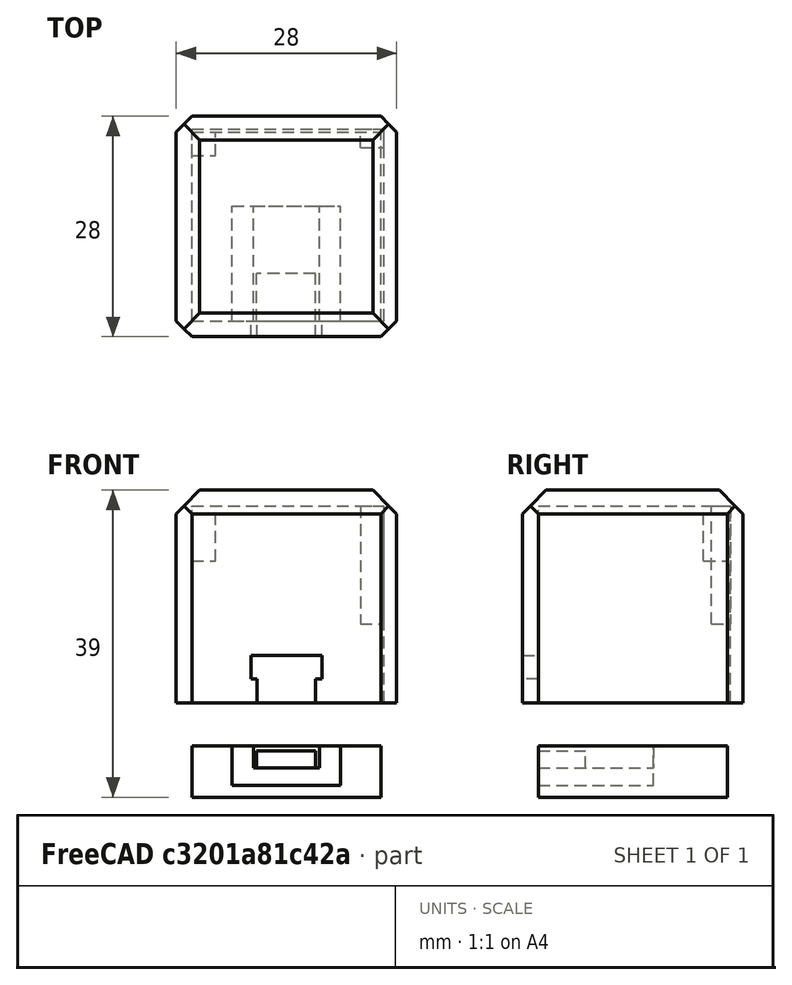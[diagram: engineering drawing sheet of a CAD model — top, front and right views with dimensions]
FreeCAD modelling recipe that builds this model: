
FCSTD DOCUMENT  (FreeCAD 0.21R33694 (Git))
Label: IR-housing
License: All rights reserved
LicenseURL: https://en.wikipedia.org/wiki/All_rights_reserved
objects: PartDesign::AdditiveBox×5, PartDesign::SubtractiveBox×5, PartDesign::Body×2, PartDesign::Chamfer×2
note: 26 computed .brp shape members not serialized (recipe doc carries the construction recipe); baked Part::Feature solids carry a one-line shape summary decoded from their .brp

FEATURE [PartDesign::AdditiveBox] Box
  AttacherType = Attacher::AttachEngine3D
  Height = 27
  Length = 28
  MapMode = 5
  Support = -> [XY_Plane]
  Width = 28
FEATURE [PartDesign::SubtractiveBox] Box001
  AttacherType = Attacher::AttachEngine3D
  AttachmentOffset = pos=(2,2,0) rot=(0,0,1;0rad)
  BaseFeature = -> Box
  Height = 25
  Length = 24.4
  MapMode = 5
  Placement = pos=(2,2,0) rot=(0,0,1;0rad)
  Support = -> [XY_Plane]
  Width = 24.4
FEATURE [PartDesign::AdditiveBox] Box002
  AttacherType = Attacher::AttachEngine3D
  AttachmentOffset = pos=(2,2,-12) rot=(0,0,1;0rad)
  Height = 6.5
  Length = 24
  MapMode = 5
  Placement = pos=(2,2,-12) rot=(0,0,1;0rad)
  Support = -> [XY_Plane001]
  Width = 24
FEATURE [PartDesign::SubtractiveBox] Box003
  AttacherType = Attacher::AttachEngine3D
  AttachmentOffset = pos=(7.1,2,-10.5) rot=(0,0,1;0rad)
  BaseFeature = -> Box002
  Height = 5
  Length = 13.8
  MapMode = 5
  Placement = pos=(7.1,2,-10.5) rot=(0,0,1;0rad)
  Support = -> [XY_Plane001]
  Width = 14.6
FEATURE [PartDesign::SubtractiveBox] Box004
  AttacherType = Attacher::AttachEngine3D
  AttachmentOffset = pos=(10.3,0,0) rot=(0,0,1;0rad)
  BaseFeature = -> Box001
  Height = 5
  Length = 7.4
  MapMode = 5
  Placement = pos=(10.3,0,0) rot=(0,0,1;0rad)
  Support = -> [XY_Plane]
  Width = 2.3
FEATURE [PartDesign::AdditiveBox] Box005
  AttacherType = Attacher::AttachEngine3D
  AttachmentOffset = pos=(9.8,2,-8.3) rot=(0,0,1;0rad)
  BaseFeature = -> Box003
  Height = 2.8
  Length = 8.4
  MapMode = 5
  Placement = pos=(9.8,2,-8.3) rot=(0,0,1;0rad)
  Support = -> [XY_Plane001]
  Width = 15.5
FEATURE [PartDesign::SubtractiveBox] Box006
  AttacherType = Attacher::AttachEngine3D
  AttachmentOffset = pos=(10.2,2,-8.5) rot=(0,0,1;0rad)
  BaseFeature = -> Box005
  Height = 2.4
  Length = 7.5
  MapMode = 5
  Placement = pos=(10.2,2,-8.5) rot=(0,0,1;0rad)
  Support = -> [XY_Plane001]
  Width = 6
FEATURE [PartDesign::Body] Body001
  Group = -> [Box002,Box003,Box005,Box006]
  Origin = -> Origin001
  Tip = -> Box006
FEATURE [PartDesign::Chamfer] Chamfer
  Angle = 45
  Base = -> Box004 [Edge2,Edge11,Edge13,Edge12]
  BaseFeature = -> Box004
  ChamferType = 0
  FlipDirection = false
  Placement = pos=(10.3,0,0) rot=(0,0,1;0rad)
  Size = 3
  Size2 = 1
  SupportTransform = false
  UseAllEdges = false
FEATURE [PartDesign::Chamfer] Chamfer001
  Angle = 45
  Base = -> Chamfer [Edge1,Edge4,Edge5,Edge24]
  BaseFeature = -> Chamfer
  ChamferType = 0
  FlipDirection = false
  Placement = pos=(10.3,0,0) rot=(0,0,1;0rad)
  Size = 2
  Size2 = 1
  SupportTransform = false
  UseAllEdges = false
FEATURE [PartDesign::AdditiveBox] Box007
  AttacherType = Attacher::AttachEngine3D
  AttachmentOffset = pos=(23.4,24,10) rot=(0,0,1;0rad)
  BaseFeature = -> Chamfer001
  Height = 15
  Length = 3
  MapMode = 5
  Placement = pos=(23.4,24,10) rot=(0,0,1;0rad)
  Support = -> [XY_Plane]
  Width = 3
FEATURE [PartDesign::AdditiveBox] Box008
  AttacherType = Attacher::AttachEngine3D
  AttachmentOffset = pos=(2,23,18) rot=(0,0,1;0rad)
  BaseFeature = -> Box007
  Height = 7
  Length = 3
  MapMode = 5
  Placement = pos=(2,23,18) rot=(0,0,1;0rad)
  Support = -> [XY_Plane]
  Width = 3
FEATURE [PartDesign::SubtractiveBox] Box009
  AttacherType = Attacher::AttachEngine3D
  AttachmentOffset = pos=(9.5,0,3) rot=(0,0,1;0rad)
  BaseFeature = -> Box008
  Height = 3
  Length = 9
  MapMode = 5
  Placement = pos=(9.5,0,3) rot=(0,0,1;0rad)
  Support = -> [XY_Plane]
  Width = 2
FEATURE [PartDesign::Body] Body
  Group = -> [Box,Box001,Box004,Chamfer,Chamfer001,Box007,Box008,Box009]
  Origin = -> Origin
  Tip = -> Box009
